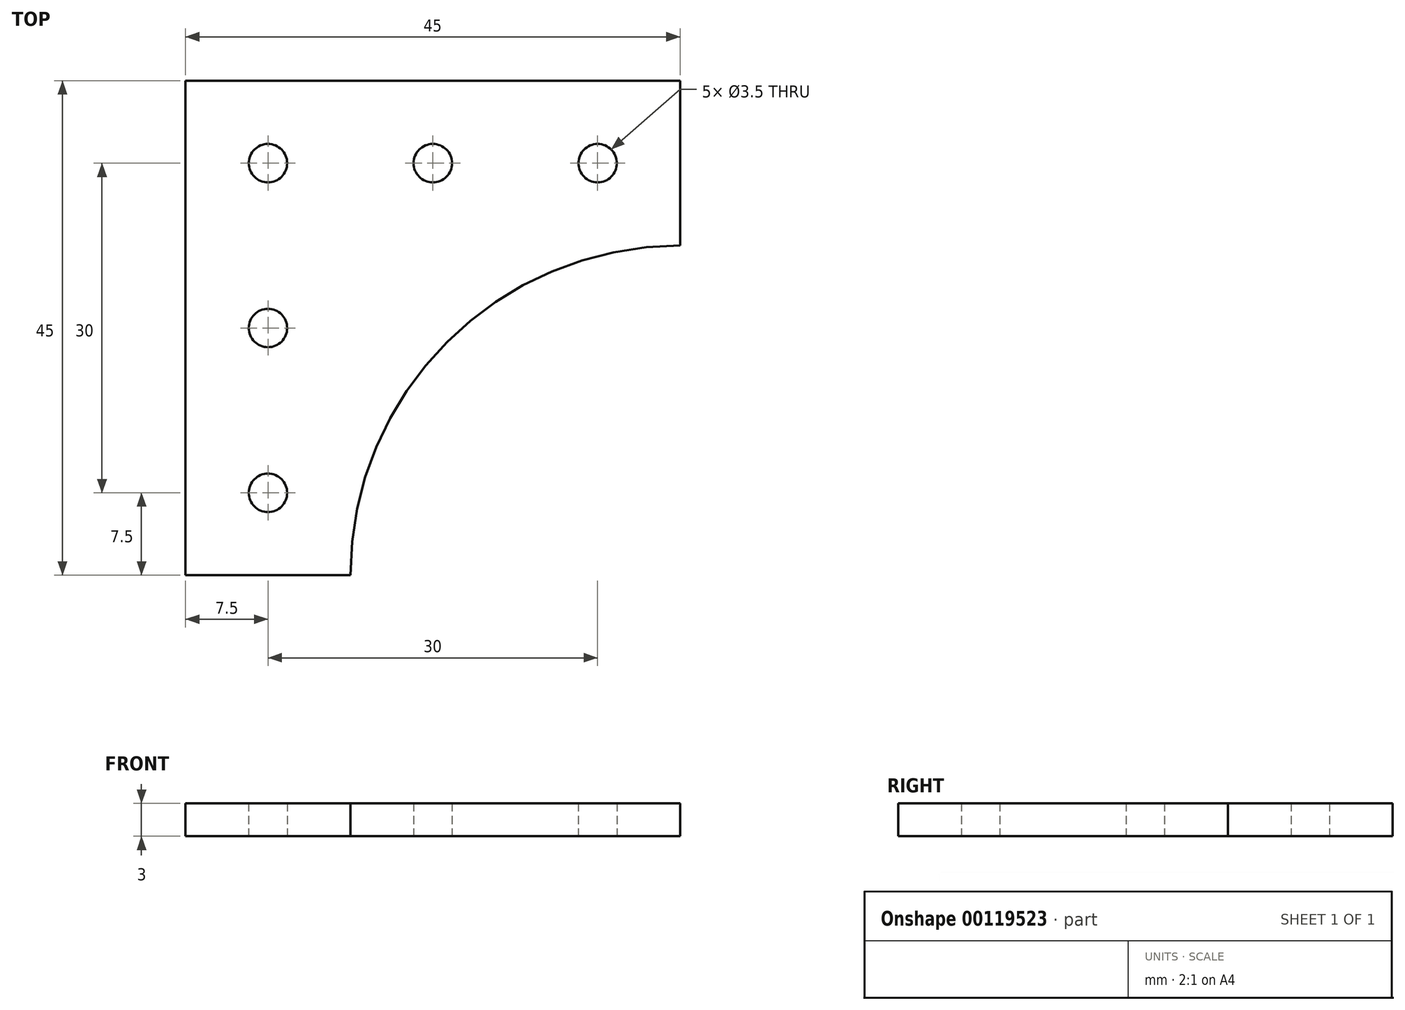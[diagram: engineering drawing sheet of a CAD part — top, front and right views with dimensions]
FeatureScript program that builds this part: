
annotation { "Feature Type Name" : "Feature", "Feature Type Description" : "" }
export const myFeature = defineFeature(function(context is Context, id is Id, definition is map)
    precondition{}
    {
        {
            var Q0;
            Q0=qCreatedBy(makeId("Top.planeOp"),FACE);
            var sketch = newSketch(context, id + "F0", { "sketchPlane" : qUnion([Q0])});
            skLineSegment(sketch, "E0.bottom", {"start": v(0, 45) * mm, "end": v(15, 45) * mm});
            skLineSegment(sketch, "E0.top", {"start": v(0, 0) * mm, "end": v(15, 0) * mm});
            skLineSegment(sketch, "E0.left", {"start": v(0, 45) * mm, "end": v(0, 30) * mm});
            skLineSegment(sketch, "E0.right", {"start": v(15, 45) * mm, "end": v(15, 0) * mm});
            skLineSegment(sketch, "E1.top", {"start": v(0, 30) * mm, "end": v(30, 30) * mm});
            skLineSegment(sketch, "E1.right", {"start": v(45, 45) * mm, "end": v(45, 30) * mm});
            skLineSegment(sketch, "E2", {"start": v(0, 30) * mm, "end": v(0, 15) * mm});
            skLineSegment(sketch, "E3", {"start": v(0, 15) * mm, "end": v(15, 15) * mm, "construction": true});
            skLineSegment(sketch, "E4", {"start": v(15, 45) * mm, "end": v(45, 45) * mm});
            skLineSegment(sketch, "E5", {"start": v(30, 45) * mm, "end": v(30, 30) * mm, "construction": true});
            skCircle(sketch, "E6", {"center": v(7.5, 37.5) * mm, "radius": 1.75 * mm});
            skPoint(sketch, "E6.centerSnap0", {"position": v(7.5, 45) * mm});
            skPoint(sketch, "E6.centerSnap1", {"position": v(30, 37.5) * mm});
            skCircle(sketch, "E7", {"center": v(7.5, 22.5) * mm, "radius": 1.75 * mm});
            skPoint(sketch, "E7.centerSnap0", {"position": v(15, 22.5) * mm});
            skLineSegment(sketch, "E8", {"start": v(0, 15) * mm, "end": v(0, 0) * mm});
            skCircle(sketch, "E9", {"center": v(7.5, 7.5) * mm, "radius": 1.75 * mm});
            skPoint(sketch, "E9.centerSnap0", {"position": v(7.5, 15) * mm});
            skPoint(sketch, "E9.centerSnap1", {"position": v(0, 7.5) * mm});
            skCircle(sketch, "E10", {"center": v(22.5, 37.5) * mm, "radius": 1.75 * mm});
            skPoint(sketch, "E10.centerSnap0", {"position": v(22.5, 30) * mm});
            skLineSegment(sketch, "E11", {"start": v(30, 30) * mm, "end": v(45, 30) * mm});
            skCircle(sketch, "E12", {"center": v(37.5, 37.5) * mm, "radius": 1.75 * mm});
            skPoint(sketch, "E12.centerSnap0", {"position": v(37.5, 30) * mm});
            skArc(sketch, "E13", {"start": v(45, 30) * mm, "mid": v(23.79, 21.21) * mm, "end": v(15, 0) * mm});
            skSolve(sketch);
        }
        {
            var Q0;
            Q0=makeQuery(id+"F0.imprint","IMPRINT",FACE,{"disambiguationData":[TD([[makeQuery(id+"F0.imprint","IMPRINT",EDGE,{"derivedFrom":sQuery(id+"F0.wireOp",EDGE,"E1.right")}),-1.0]])]});
            var Q1;
            {var subQ4=sQuery(id+"F0.wireOp",EDGE,"E0.bottom");Q1=makeQuery(id+"F0.imprint","IMPRINT",FACE,{"disambiguationData":[TD([[makeQuery(id+"F0.imprint","IMPRINT",EDGE,{"derivedFrom":subQ4}),-1.0]])]});}
            var Q2;
            {var subQ4=sQuery(id+"F0.wireOp",EDGE,"E0.top");Q2=makeQuery(id+"F0.imprint","IMPRINT",FACE,{"disambiguationData":[TD([[makeQuery(id+"F0.imprint","IMPRINT",EDGE,{"derivedFrom":subQ4}),1.0]])]});}
            var Q3;
            {var subQ4=sQuery(id+"F0.wireOp",EDGE,"E11");Q3=makeQuery(id+"F0.imprint","IMPRINT",FACE,{"disambiguationData":[TD([[makeQuery(id+"F0.imprint","IMPRINT",EDGE,{"derivedFrom":subQ4}),-1.0]])]});}
            extrude(context, id + "F1", {"entities" : qUnion([Q0, Q1, Q2, Q3]), "depth" : 3 * mm});
        }
    });
